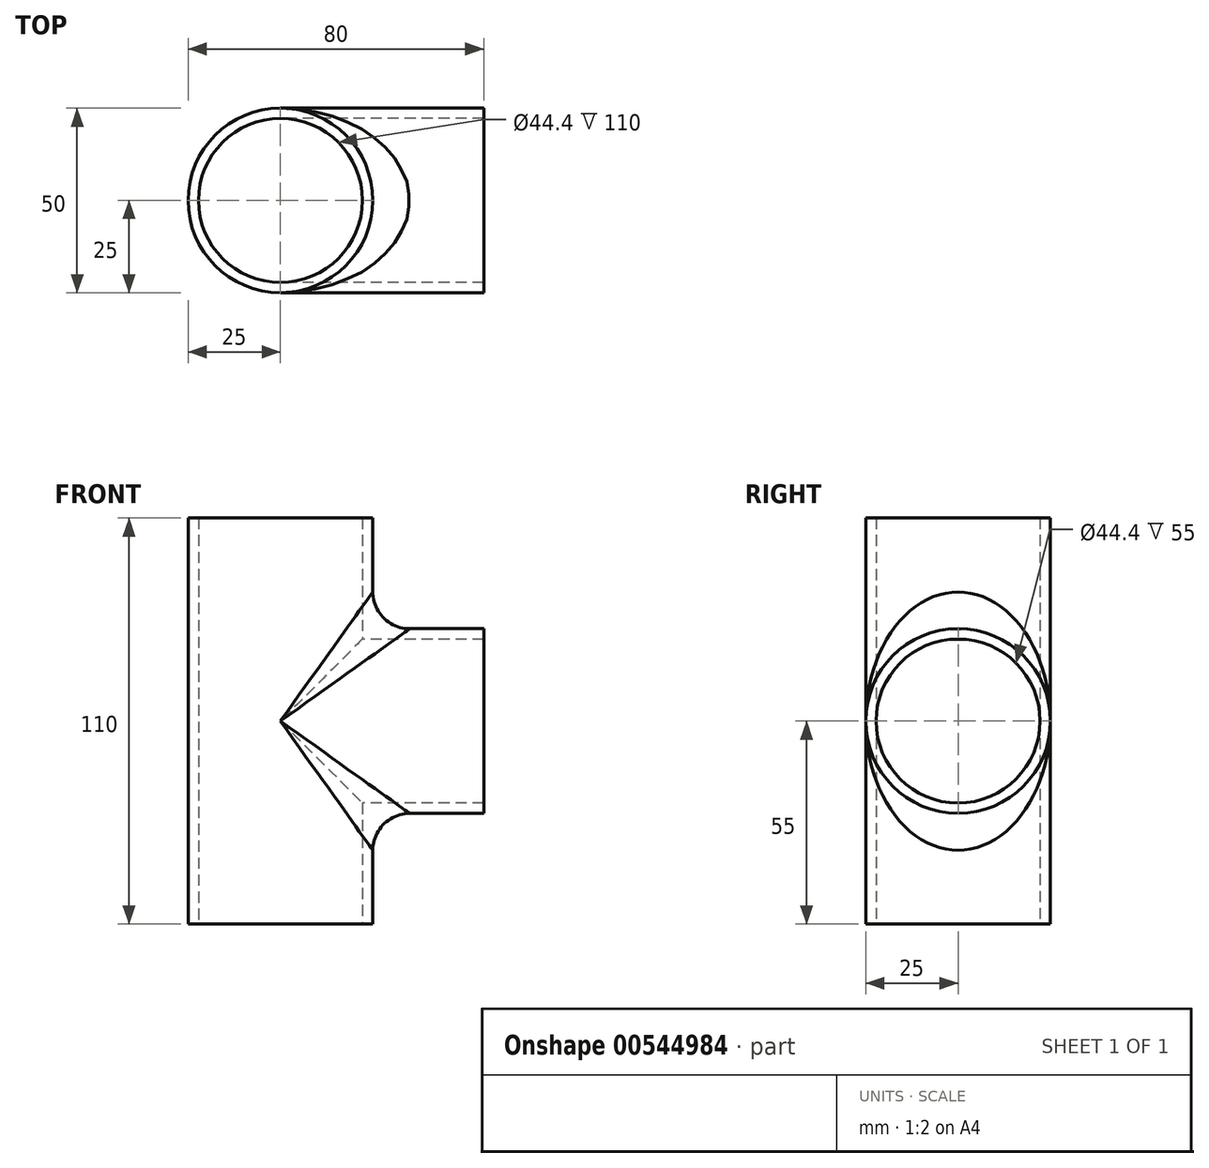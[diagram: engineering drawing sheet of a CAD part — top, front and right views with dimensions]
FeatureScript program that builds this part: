
annotation { "Feature Type Name" : "Feature", "Feature Type Description" : "" }
export const myFeature = defineFeature(function(context is Context, id is Id, definition is map)
    precondition{}
    {
        {
            var Q0;
            Q0=qCreatedBy(makeId("Top.planeOp"),FACE);
            var sketch = newSketch(context, id + "F0", { "sketchPlane" : qUnion([Q0])});
            skCircle(sketch, "E0", {"center": v(0, 0) * mm, "radius": 25 * mm});
            skCircle(sketch, "E1", {"center": v(0, 0) * mm, "radius": 22.2 * mm});
            skSolve(sketch);
        }
        {
            var Q0;
            Q0=makeQuery(id+"F0.imprint","IMPRINT",FACE,{"disambiguationData":[TD([[makeQuery(id+"F0.imprint","IMPRINT",EDGE,{"derivedFrom":sQuery(id+"F0.wireOp",EDGE,"E0")}),1.0]])]});
            extrude(context, id + "F1", {"entities" : qUnion([Q0]), "depth" : 110 * mm, "offsetDistance" : 25 * mm});
        }
        {
            var Q0;
            Q0=qCreatedBy(makeId("Right.planeOp"),FACE);
            cPlane(context, id + "F2", {"entities" : qUnion([Q0]), "cplaneType" : CPlaneType.OFFSET, "offset" : 25 * mm, "width" : 150 * mm, "height" : 150 * mm});
        }
        {
            var Q0;
            Q0=qCreatedBy(id+"F2.planeOp",FACE);
            var sketch = newSketch(context, id + "F3", { "sketchPlane" : qUnion([Q0])});
            skCircle(sketch, "E2", {"center": v(0, 55) * mm, "radius": 25 * mm});
            skCircle(sketch, "E3", {"center": v(0, 55) * mm, "radius": 22.2 * mm});
            skSolve(sketch);
        }
        {
            var Q0;
            Q0=makeQuery(id+"F3.imprint","IMPRINT",FACE,{"disambiguationData":[TD([[makeQuery(id+"F3.imprint","IMPRINT",EDGE,{"derivedFrom":sQuery(id+"F3.wireOp",EDGE,"E2")}),1.0]])]});
            var Q1;
            Q1=makeQuery(id+"F1.opExtrude","SWEPT_FACE",FACE,{"disambiguationData":[OSD([sQuery(id+"F0.wireOp",EDGE,"E0")])]});
            extrude(context, id + "F4", {"entities" : qUnion([Q0]), "operationType" : NewBodyOperationType.ADD, "depth" : 30 * mm, "offsetDistance" : 25 * mm, "hasSecondDirection" : true, "secondDirectionBound" : SecondDirectionBoundingType.UP_TO_SURFACE, "secondDirectionOppositeDirection" : true, "secondDirectionDepth" : 25 * mm, "secondDirectionBoundEntityFace" : qUnion([Q1])});
        }
        {
            var Q0;
            Q0=makeQuery(id+"F3.imprint","IMPRINT",FACE,{"disambiguationData":[TD([[makeQuery(id+"F3.imprint","IMPRINT",EDGE,{"derivedFrom":sQuery(id+"F3.wireOp",EDGE,"E3")}),1.0]])]});
            extrude(context, id + "F5", {"entities" : qUnion([Q0]), "operationType" : NewBodyOperationType.REMOVE, "oppositeDirection" : true, "depth" : 25 * mm, "offsetDistance" : 25 * mm});
        }
        {
            var Q0;
            Q0=makeQuery(id+"F4.opExtrude","CAP_EDGE",EDGE,{"disambiguationData":[OSD([sQuery(id+"F3.wireOp",EDGE,"E2")]),topologyDisambiguationEdgeConnected([makeQuery(id+"F1.opExtrude","SWEPT_FACE",FACE,{"disambiguationData":[OSD([sQuery(id+"F0.wireOp",EDGE,"E0")])]})]),OD(1.0)],"isStart":false});
            var Q1;
            Q1=makeQuery(id+"F4.opExtrude","CAP_EDGE",EDGE,{"disambiguationData":[OSD([sQuery(id+"F3.wireOp",EDGE,"E2")]),topologyDisambiguationEdgeConnected([makeQuery(id+"F1.opExtrude","SWEPT_FACE",FACE,{"disambiguationData":[OSD([sQuery(id+"F0.wireOp",EDGE,"E0")])]})]),OD(0.0)],"isStart":false});
            fillet(context, id + "F6", {"entities" : qUnion([Q0, Q1]), "radius" : 10 * mm, "tangentPropagation" : true, "allowEdgeOverflow" : false});
        }
    });
